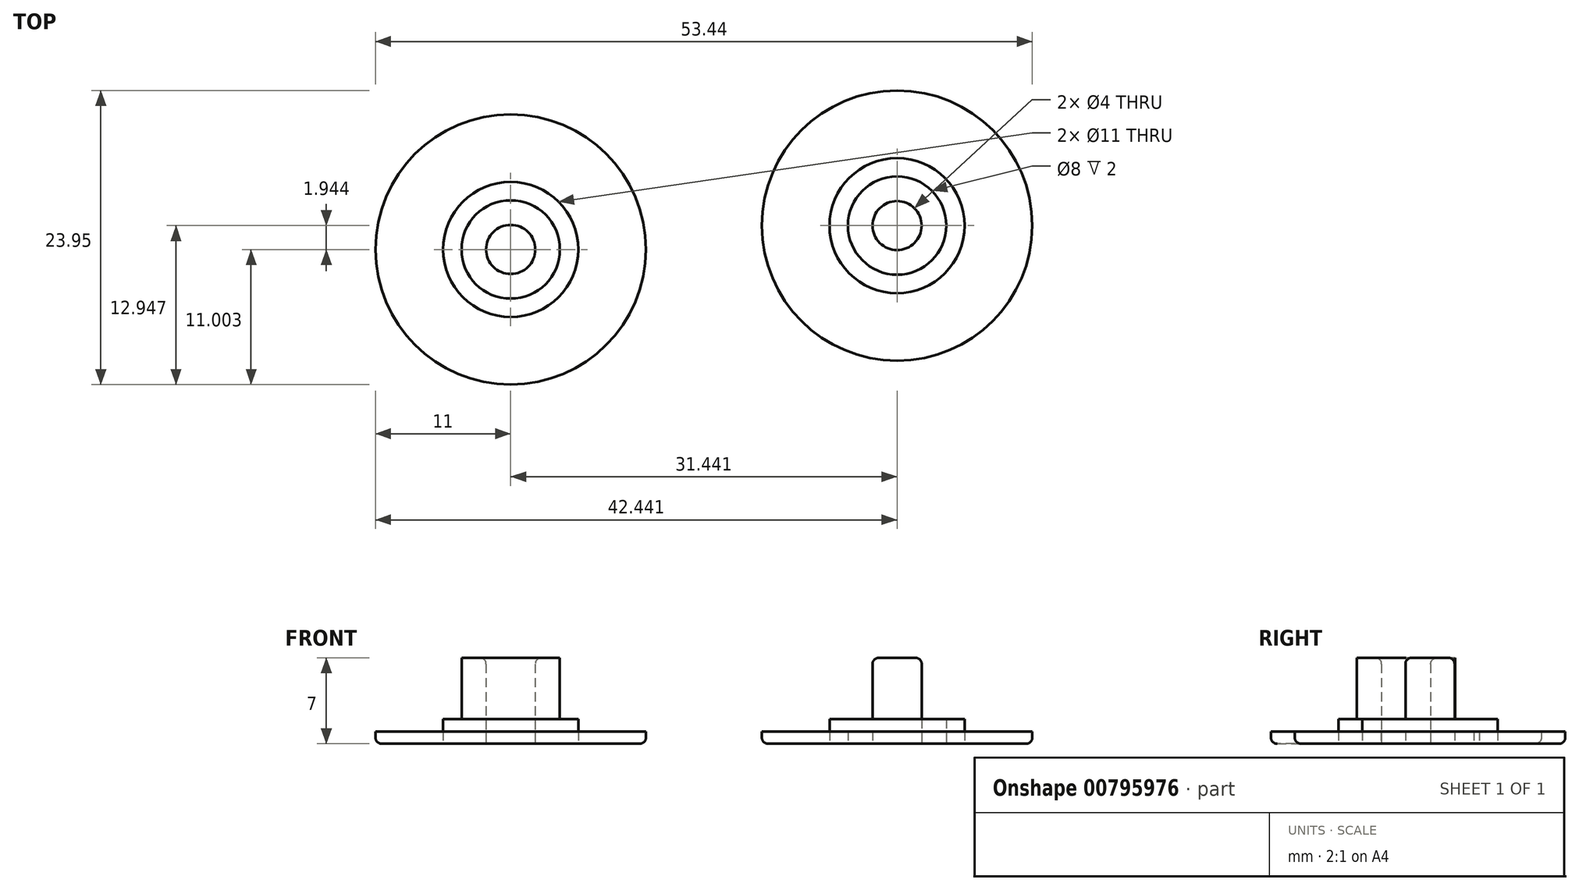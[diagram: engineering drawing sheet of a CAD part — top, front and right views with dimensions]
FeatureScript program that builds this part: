
annotation { "Feature Type Name" : "Feature", "Feature Type Description" : "" }
export const myFeature = defineFeature(function(context is Context, id is Id, definition is map)
    precondition{}
    {
        {
            var Q0;
            Q0=qCreatedBy(makeId("Top.planeOp"),FACE);
            var sketch = newSketch(context, id + "F0", { "sketchPlane" : qUnion([Q0])});
            skCircle(sketch, "E0", {"center": v(15.24, -0.53) * mm, "radius": 11 * mm});
            skCircle(sketch, "E1", {"center": v(15.24, -0.53) * mm, "radius": 5.5 * mm});
            skCircle(sketch, "E2", {"center": v(15.24, -0.53) * mm, "radius": 4 * mm});
            skCircle(sketch, "E3", {"center": v(15.24, -0.53) * mm, "radius": 2 * mm});
            skCircle(sketch, "E4", {"center": v(-16.2, -2.48) * mm, "radius": 11 * mm});
            skCircle(sketch, "E5", {"center": v(-16.2, -2.48) * mm, "radius": 5.5 * mm});
            skCircle(sketch, "E6", {"center": v(-16.2, -2.48) * mm, "radius": 4 * mm});
            skCircle(sketch, "E7", {"center": v(-16.2, -2.48) * mm, "radius": 2 * mm});
            skSolve(sketch);
        }
        {
            var Q0;
            Q0=makeQuery(id+"F0.imprint","IMPRINT",FACE,{"disambiguationData":[TD([[makeQuery(id+"F0.imprint","IMPRINT",EDGE,{"derivedFrom":sQuery(id+"F0.wireOp",EDGE,"E0")}),1.0]])]});
            extrude(context, id + "F1", {"entities" : qUnion([Q0]), "depth" : 1 * mm, "offsetDistance" : 25 * mm});
        }
        {
            var Q0;
            Q0=makeQuery(id+"F0.imprint","IMPRINT",FACE,{"disambiguationData":[TD([[makeQuery(id+"F0.imprint","IMPRINT",EDGE,{"derivedFrom":sQuery(id+"F0.wireOp",EDGE,"E4")}),1.0]])]});
            extrude(context, id + "F2", {"entities" : qUnion([Q0]), "depth" : 1 * mm, "offsetDistance" : 25 * mm});
        }
        {
            var Q0;
            Q0=makeQuery(id+"F0.imprint","IMPRINT",FACE,{"disambiguationData":[TD([[makeQuery(id+"F0.imprint","IMPRINT",EDGE,{"derivedFrom":sQuery(id+"F0.wireOp",EDGE,"E5")}),1.0]])]});
            var Q1;
            Q1=makeQuery(id+"F0.imprint","IMPRINT",FACE,{"disambiguationData":[TD([[makeQuery(id+"F0.imprint","IMPRINT",EDGE,{"derivedFrom":sQuery(id+"F0.wireOp",EDGE,"E1")}),1.0]])]});
            extrude(context, id + "F3", {"entities" : qUnion([Q0, Q1]), "depth" : 2 * mm, "offsetDistance" : 25 * mm});
        }
        {
            var Q0;
            Q0=makeQuery(id+"F0.imprint","IMPRINT",FACE,{"disambiguationData":[TD([[makeQuery(id+"F0.imprint","IMPRINT",EDGE,{"derivedFrom":sQuery(id+"F0.wireOp",EDGE,"E6")}),1.0]])]});
            var Q1;
            Q1=makeQuery(id+"F0.imprint","IMPRINT",FACE,{"disambiguationData":[TD([[makeQuery(id+"F0.imprint","IMPRINT",EDGE,{"derivedFrom":sQuery(id+"F0.wireOp",EDGE,"E3")}),1.0]])]});
            extrude(context, id + "F4", {"entities" : qUnion([Q0, Q1]), "operationType" : NewBodyOperationType.ADD, "depth" : 7 * mm, "offsetDistance" : 25 * mm});
        }
        {
            var Q0;
            Q0=makeQuery(id+"F0.imprint","IMPRINT",FACE,{"disambiguationData":[TD([[makeQuery(id+"F0.imprint","IMPRINT",EDGE,{"derivedFrom":sQuery(id+"F0.wireOp",EDGE,"E7")}),1.0]])]});
            var Q1;
            Q1=makeQuery(id+"F0.imprint","IMPRINT",FACE,{"disambiguationData":[TD([[makeQuery(id+"F0.imprint","IMPRINT",EDGE,{"derivedFrom":sQuery(id+"F0.wireOp",EDGE,"E2")}),1.0]])]});
            extrude(context, id + "F5", {"entities" : qUnion([Q0, Q1]), "depth" : 1 * mm, "offsetDistance" : 25 * mm});
        }
        {
            var Q0;
            Q0=makeQuery(id+"F1.opExtrude","CAP_EDGE",EDGE,{"disambiguationData":[OSD([sQuery(id+"F0.wireOp",EDGE,"E0")])],"isStart":true});
            var Q1;
            Q1=makeQuery(id+"F2.opExtrude","CAP_EDGE",EDGE,{"disambiguationData":[OSD([sQuery(id+"F0.wireOp",EDGE,"E4")])],"isStart":true});
            fillet(context, id + "F6", {"entities" : qUnion([Q0, Q1]), "radius" : 0.5 * mm, "tangentPropagation" : true, "allowEdgeOverflow" : false});
        }
        {
            var Q0;
            Q0=makeQuery(id+"F4.opExtrude","CAP_EDGE",EDGE,{"disambiguationData":[OSD([sQuery(id+"F0.wireOp",EDGE,"E3")])],"isStart":false});
            var Q1;
            Q1=makeQuery(id+"F4.opExtrude","CAP_EDGE",EDGE,{"disambiguationData":[OSD([sQuery(id+"F0.wireOp",EDGE,"E7")])],"isStart":false});
            fillet(context, id + "F7", {"entities" : qUnion([Q0, Q1]), "radius" : 0.5 * mm, "tangentPropagation" : true, "allowEdgeOverflow" : false});
        }
    });
